# Revit family: WVA-8
name_source: partatom
category: Mechanical Equipment
revit_build: Autodesk Revit MEP 2014 (Build: 20140709_2115(x64)
units: mm (PartAtom-declared; Revit-internal decimal feet)

## types (1)
- WVA-8
    A = 23 1/2"
    ApproximateShipmentWeight = 700 lbs
    ArrayRadius = 10 1/4"
    B = 49"
    BottomExtrusionHeight = 1/2"
    BottomRevolveHeight = 5 3/8"
    C = 33 5/8"
    CouplingHeight = 7 5/8"
    CylindarDia = 16 1/2"
    CylinderHalfLength = 11 3/4"
    CylinderHeight = 38 1/4"
    D = 24 1/2"
    DrainExtrusionPosition = 1 3/4"
    Height1 = 1 5/8"
    Height2 = 1/4"
    HookDiameter = 1/2"
    HookDistance = 4 5/8"
    HookTopDistance = 5/8"
    HookWidth = 1 7/8"
    LeftHookDistance = 1 1/8"
    Manufacturer = Wessels Company
    MaximumFlow = 945 GPM
    MaximumOperatingPressure = 125 PSIG
    MaximumOperatingTemperature = 240°F
    Model = WVA-8
    NumberOfArray = 9
    PartNumber = 72080080
    PipeConnectorDiameter = 8"
    PipeDiameter = 8 5/8"
    RevolveRadius = 8 1/4"
    RingDistance = 9 5/8"
    SideDrainExtrusion = 1 1/2"
    SideFlangeStep1 = 9 5/8"
    SideFlangeStep2 = 13 5/8"
    SideFlangeThickness = 1 1/8"
    SideFlangeThickness1 = 5/8"
    Step1Diameter = 1 1/4"
    Step2Diameter = 2 5/8"
    Step3Diameter = 4 1/4"
    Step4Diameter = 6"
    Step5Diameter = 5 1/8"
    TopExtrusionDiameter = 2 5/8"
    TotalHeight = 6 5/8"
    URL = http://westank.com

## geometry (parser evidence)
native form markers: Extrusion x4, Revolve x2, Sweep x5
no freeform markers — native parametric forms only
